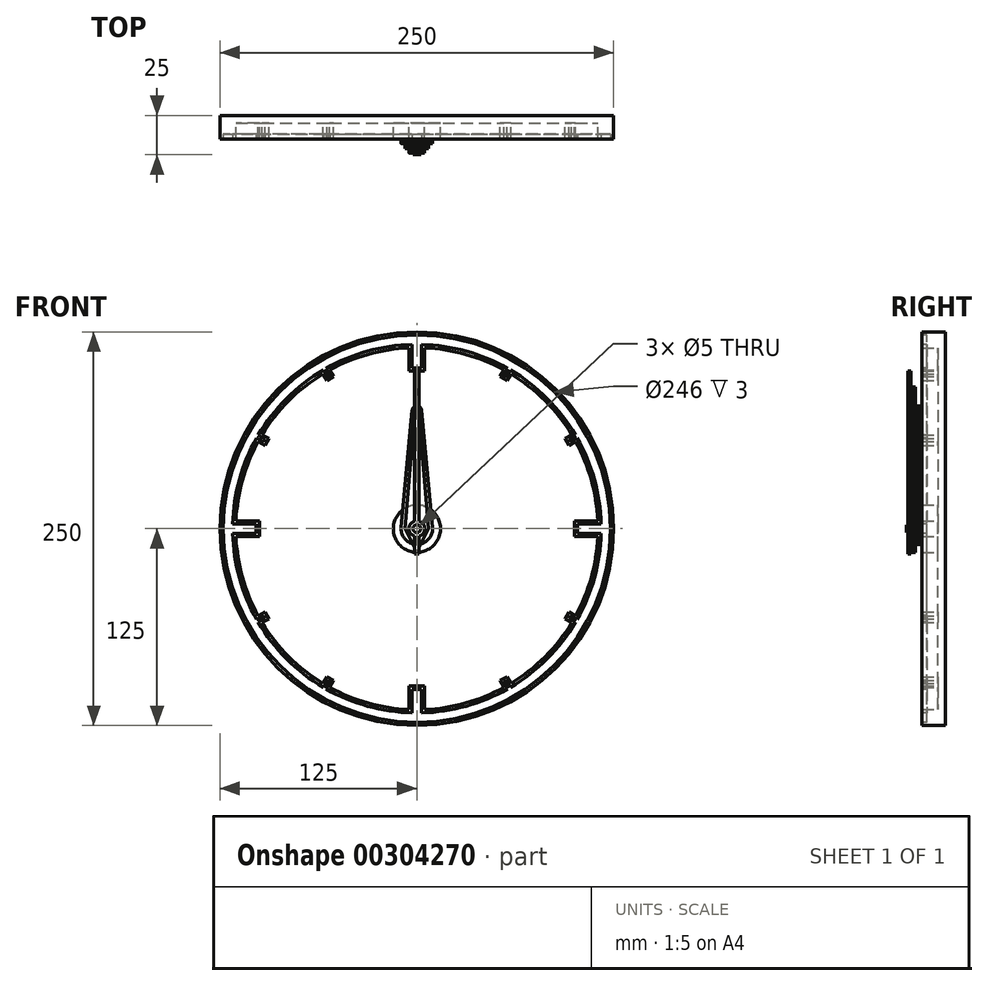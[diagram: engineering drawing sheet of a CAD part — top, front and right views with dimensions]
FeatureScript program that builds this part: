
annotation { "Feature Type Name" : "Feature", "Feature Type Description" : "" }
export const myFeature = defineFeature(function(context is Context, id is Id, definition is map)
    precondition{}
    {
        {
            var Q0;
            Q0=qCreatedBy(makeId("Front.planeOp"),FACE);
            var sketch = newSketch(context, id + "F0", { "sketchPlane" : qUnion([Q0])});
            skCircle(sketch, "E0", {"center": v(0, 0) * mm, "radius": 125 * mm});
            skSolve(sketch);
        }
        {
            var Q0;
            Q0 = qSketchRegion(id + "F0", true);
            extrude(context, id + "F1", {"entities" : qUnion([Q0]), "oppositeDirection" : true, "depth" : 5 * mm});
        }
        {
            var Q0;
            Q0=makeQuery(id+"F1.opExtrude","CAP_FACE",FACE,{"disambiguationData":[OSD([sQuery(id+"F0.wireOp",EDGE,"E0")])],"isStart":true});
            var sketch = newSketch(context, id + "F2", { "sketchPlane" : qUnion([Q0])});
            skCircle(sketch, "E1", {"center": v(0, 0) * mm, "radius": 15 * mm});
            skSolve(sketch);
        }
        {
            var Q0;
            Q0 = qSketchRegion(id + "F2", true);
            extrude(context, id + "F3", {"entities" : qUnion([Q0]), "depth" : 10 * mm});
        }
        {
            var Q0;
            Q0=makeQuery(id+"F3.opExtrude","CAP_FACE",FACE,{"disambiguationData":[OSD([sQuery(id+"F2.wireOp",EDGE,"E1")])],"isStart":false});
            var sketch = newSketch(context, id + "F4", { "sketchPlane" : qUnion([Q0])});
            skCircle(sketch, "E2", {"center": v(0, 0) * mm, "radius": 2.5 * mm});
            skSolve(sketch);
        }
        {
            var Q0;
            Q0 = qSketchRegion(id + "F4", true);
            extrude(context, id + "F5", {"entities" : qUnion([Q0]), "operationType" : NewBodyOperationType.ADD, "depth" : 10 * mm});
        }
        {
            var Q0;
            Q0=makeQuery(id+"F1.opExtrude","CAP_FACE",FACE,{"disambiguationData":[OSD([sQuery(id+"F0.wireOp",EDGE,"E0")])],"isStart":true});
            var sketch = newSketch(context, id + "F6", { "sketchPlane" : qUnion([Q0])});
            skCircle(sketch, "E3.0", {"center": v(0, 0) * mm, "radius": 125 * mm});
            skCircle(sketch, "E4", {"center": v(0, 0) * mm, "radius": 115 * mm});
            skSolve(sketch);
        }
        {
            var Q0;
            Q0 = qSketchRegion(id + "F6", true);
            extrude(context, id + "F7", {"entities" : qUnion([Q0]), "depth" : 10 * mm});
        }
        {
            var Q0;
            Q0=makeQuery(id+"F1.opExtrude","CAP_FACE",FACE,{"disambiguationData":[OSD([sQuery(id+"F0.wireOp",EDGE,"E0")])],"isStart":true});
            var sketch = newSketch(context, id + "F8", { "sketchPlane" : qUnion([Q0])});
            skLineSegment(sketch, "E5.bottom", {"start": v(5, 100) * mm, "end": v(-5, 100) * mm});
            skLineSegment(sketch, "E5.top", {"start": v(5, 120) * mm, "end": v(-5, 120) * mm});
            skLineSegment(sketch, "E5.left", {"start": v(5, 100) * mm, "end": v(5, 120) * mm});
            skLineSegment(sketch, "E5.right", {"start": v(-5, 100) * mm, "end": v(-5, 120) * mm});
            skPoint(sketch, "E5.middle", {"position": v(0, 110) * mm});
            skLineSegment(sketch, "E6.1.0", {"start": v(-100, 5) * mm, "end": v(-100, -5) * mm});
            skLineSegment(sketch, "E6.1.1", {"start": v(-120, 5) * mm, "end": v(-120, -5) * mm});
            skLineSegment(sketch, "E6.1.2", {"start": v(-100, 5) * mm, "end": v(-120, 5) * mm});
            skLineSegment(sketch, "E6.1.3", {"start": v(-100, -5) * mm, "end": v(-120, -5) * mm});
            skPoint(sketch, "E6.1.4", {"position": v(-110, 0) * mm});
            skLineSegment(sketch, "E6.2.0", {"start": v(-5, -100) * mm, "end": v(5, -100) * mm});
            skLineSegment(sketch, "E6.2.1", {"start": v(-5, -120) * mm, "end": v(5, -120) * mm});
            skLineSegment(sketch, "E6.2.2", {"start": v(-5, -100) * mm, "end": v(-5, -120) * mm});
            skLineSegment(sketch, "E6.2.3", {"start": v(5, -100) * mm, "end": v(5, -120) * mm});
            skPoint(sketch, "E6.2.4", {"position": v(0, -110) * mm});
            skLineSegment(sketch, "E6.3.0", {"start": v(100, -5) * mm, "end": v(100, 5) * mm});
            skLineSegment(sketch, "E6.3.1", {"start": v(120, -5) * mm, "end": v(120, 5) * mm});
            skLineSegment(sketch, "E6.3.2", {"start": v(100, -5) * mm, "end": v(120, -5) * mm});
            skLineSegment(sketch, "E6.3.3", {"start": v(100, 5) * mm, "end": v(120, 5) * mm});
            skPoint(sketch, "E6.3.4", {"position": v(110, 0) * mm});
            skPoint(sketch, "E6.center", {"position": v(0, 0) * mm});
            skSolve(sketch);
        }
        {
            var Q0;
            Q0 = qSketchRegion(id + "F8", true);
            extrude(context, id + "F9", {"entities" : qUnion([Q0]), "operationType" : NewBodyOperationType.ADD, "depth" : 10 * mm});
        }
        {
            var Q0;
            Q0=makeQuery(id+"F1.opExtrude","CAP_FACE",FACE,{"disambiguationData":[OSD([sQuery(id+"F0.wireOp",EDGE,"E0")])],"isStart":true});
            var sketch = newSketch(context, id + "F10", { "sketchPlane" : qUnion([Q0])});
            skLineSegment(sketch, "E7", {"start": v(0, 0) * mm, "end": v(0, 87.81) * mm, "construction": true});
            skLineSegment(sketch, "E8", {"start": v(0, 0) * mm, "end": v(55, 95.26) * mm, "construction": true});
            skLineSegment(sketch, "E9", {"start": v(0, 0) * mm, "end": v(95.26, 55) * mm, "construction": true});
            skLineSegment(sketch, "E10", {"start": v(57.83, 105.17) * mm, "end": v(52.83, 96.51) * mm});
            skLineSegment(sketch, "E11", {"start": v(52.83, 96.51) * mm, "end": v(57.17, 94.01) * mm});
            skLineSegment(sketch, "E12", {"start": v(57.17, 94.01) * mm, "end": v(62.17, 102.67) * mm});
            skLineSegment(sketch, "E13", {"start": v(62.17, 102.67) * mm, "end": v(57.83, 105.17) * mm});
            skLineSegment(sketch, "E14", {"start": v(102.67, 62.17) * mm, "end": v(94.01, 57.17) * mm});
            skLineSegment(sketch, "E15", {"start": v(94.01, 57.17) * mm, "end": v(96.51, 52.83) * mm});
            skLineSegment(sketch, "E16", {"start": v(96.51, 52.83) * mm, "end": v(105.17, 57.83) * mm});
            skLineSegment(sketch, "E17", {"start": v(105.17, 57.83) * mm, "end": v(102.67, 62.17) * mm});
            skLineSegment(sketch, "E18.1.0", {"start": v(-105.17, 57.83) * mm, "end": v(-96.51, 52.83) * mm});
            skLineSegment(sketch, "E18.1.1", {"start": v(-96.51, 52.83) * mm, "end": v(-94.01, 57.17) * mm});
            skLineSegment(sketch, "E18.1.2", {"start": v(-94.01, 57.17) * mm, "end": v(-102.67, 62.17) * mm});
            skLineSegment(sketch, "E18.1.3", {"start": v(-102.67, 62.17) * mm, "end": v(-105.17, 57.83) * mm});
            skLineSegment(sketch, "E18.1.4", {"start": v(-62.17, 102.67) * mm, "end": v(-57.17, 94.01) * mm});
            skLineSegment(sketch, "E18.1.5", {"start": v(-57.17, 94.01) * mm, "end": v(-52.83, 96.51) * mm});
            skLineSegment(sketch, "E18.1.6", {"start": v(-57.83, 105.17) * mm, "end": v(-62.17, 102.67) * mm});
            skLineSegment(sketch, "E18.1.7", {"start": v(-52.83, 96.51) * mm, "end": v(-57.83, 105.17) * mm});
            skLineSegment(sketch, "E18.2.0", {"start": v(-57.83, -105.17) * mm, "end": v(-52.83, -96.51) * mm});
            skLineSegment(sketch, "E18.2.1", {"start": v(-52.83, -96.51) * mm, "end": v(-57.17, -94.01) * mm});
            skLineSegment(sketch, "E18.2.2", {"start": v(-57.17, -94.01) * mm, "end": v(-62.17, -102.67) * mm});
            skLineSegment(sketch, "E18.2.3", {"start": v(-62.17, -102.67) * mm, "end": v(-57.83, -105.17) * mm});
            skLineSegment(sketch, "E18.2.4", {"start": v(-102.67, -62.17) * mm, "end": v(-94.01, -57.17) * mm});
            skLineSegment(sketch, "E18.2.5", {"start": v(-94.01, -57.17) * mm, "end": v(-96.51, -52.83) * mm});
            skLineSegment(sketch, "E18.2.6", {"start": v(-105.17, -57.83) * mm, "end": v(-102.67, -62.17) * mm});
            skLineSegment(sketch, "E18.2.7", {"start": v(-96.51, -52.83) * mm, "end": v(-105.17, -57.83) * mm});
            skLineSegment(sketch, "E18.3.0", {"start": v(105.17, -57.83) * mm, "end": v(96.51, -52.83) * mm});
            skLineSegment(sketch, "E18.3.1", {"start": v(96.51, -52.83) * mm, "end": v(94.01, -57.17) * mm});
            skLineSegment(sketch, "E18.3.2", {"start": v(94.01, -57.17) * mm, "end": v(102.67, -62.17) * mm});
            skLineSegment(sketch, "E18.3.3", {"start": v(102.67, -62.17) * mm, "end": v(105.17, -57.83) * mm});
            skLineSegment(sketch, "E18.3.4", {"start": v(62.17, -102.67) * mm, "end": v(57.17, -94.01) * mm});
            skLineSegment(sketch, "E18.3.5", {"start": v(57.17, -94.01) * mm, "end": v(52.83, -96.51) * mm});
            skLineSegment(sketch, "E18.3.6", {"start": v(57.83, -105.17) * mm, "end": v(62.17, -102.67) * mm});
            skLineSegment(sketch, "E18.3.7", {"start": v(52.83, -96.51) * mm, "end": v(57.83, -105.17) * mm});
            skPoint(sketch, "E18.center", {"position": v(0, 0) * mm});
            skSolve(sketch);
        }
        {
            var Q0;
            Q0 = qSketchRegion(id + "F10", true);
            extrude(context, id + "F11", {"entities" : qUnion([Q0]), "operationType" : NewBodyOperationType.ADD, "depth" : 10 * mm});
        }
        {
            var Q0;
            Q0=makeQuery(id+"F11.boolean.opBoolean","MERGE",FACE,{"derivedFrom":[makeQuery(id+"F9.boolean.opBoolean","MERGE",FACE,{"derivedFrom":[makeQuery(id+"F7.opExtrude","CAP_FACE",FACE,{"disambiguationData":[OSD([sQuery(id+"F6.wireOp",EDGE,"E3.0"),sQuery(id+"F6.wireOp",EDGE,"E4")])],"isStart":false}),makeQuery(id+"F9.opExtrude","CAP_FACE",FACE,{"disambiguationData":[OSD([sQuery(id+"F8.wireOp",EDGE,"E5.bottom"),sQuery(id+"F8.wireOp",EDGE,"E5.top"),sQuery(id+"F8.wireOp",EDGE,"E5.left"),sQuery(id+"F8.wireOp",EDGE,"E5.right")])],"isStart":false}),makeQuery(id+"F9.opExtrude","CAP_FACE",FACE,{"disambiguationData":[OSD([sQuery(id+"F8.wireOp",EDGE,"E6.1.0"),sQuery(id+"F8.wireOp",EDGE,"E6.1.1"),sQuery(id+"F8.wireOp",EDGE,"E6.1.2"),sQuery(id+"F8.wireOp",EDGE,"E6.1.3")])],"isStart":false}),makeQuery(id+"F9.opExtrude","CAP_FACE",FACE,{"disambiguationData":[OSD([sQuery(id+"F8.wireOp",EDGE,"E6.2.0"),sQuery(id+"F8.wireOp",EDGE,"E6.2.1"),sQuery(id+"F8.wireOp",EDGE,"E6.2.2"),sQuery(id+"F8.wireOp",EDGE,"E6.2.3")])],"isStart":false}),makeQuery(id+"F9.opExtrude","CAP_FACE",FACE,{"disambiguationData":[OSD([sQuery(id+"F8.wireOp",EDGE,"E6.3.0"),sQuery(id+"F8.wireOp",EDGE,"E6.3.1"),sQuery(id+"F8.wireOp",EDGE,"E6.3.2"),sQuery(id+"F8.wireOp",EDGE,"E6.3.3")])],"isStart":false})]}),makeQuery(id+"F11.opExtrude","CAP_FACE",FACE,{"disambiguationData":[OSD([sQuery(id+"F10.wireOp",EDGE,"E10"),sQuery(id+"F10.wireOp",EDGE,"E11"),sQuery(id+"F10.wireOp",EDGE,"E12"),sQuery(id+"F10.wireOp",EDGE,"E13")])],"isStart":false}),makeQuery(id+"F11.opExtrude","CAP_FACE",FACE,{"disambiguationData":[OSD([sQuery(id+"F10.wireOp",EDGE,"E14"),sQuery(id+"F10.wireOp",EDGE,"E15"),sQuery(id+"F10.wireOp",EDGE,"E16"),sQuery(id+"F10.wireOp",EDGE,"E17")])],"isStart":false}),makeQuery(id+"F11.opExtrude","CAP_FACE",FACE,{"disambiguationData":[OSD([sQuery(id+"F10.wireOp",EDGE,"E18.1.0"),sQuery(id+"F10.wireOp",EDGE,"E18.1.1"),sQuery(id+"F10.wireOp",EDGE,"E18.1.2"),sQuery(id+"F10.wireOp",EDGE,"E18.1.3")])],"isStart":false}),makeQuery(id+"F11.opExtrude","CAP_FACE",FACE,{"disambiguationData":[OSD([sQuery(id+"F10.wireOp",EDGE,"E18.1.4"),sQuery(id+"F10.wireOp",EDGE,"E18.1.5"),sQuery(id+"F10.wireOp",EDGE,"E18.1.6"),sQuery(id+"F10.wireOp",EDGE,"E18.1.7")])],"isStart":false}),makeQuery(id+"F11.opExtrude","CAP_FACE",FACE,{"disambiguationData":[OSD([sQuery(id+"F10.wireOp",EDGE,"E18.2.0"),sQuery(id+"F10.wireOp",EDGE,"E18.2.1"),sQuery(id+"F10.wireOp",EDGE,"E18.2.2"),sQuery(id+"F10.wireOp",EDGE,"E18.2.3")])],"isStart":false}),makeQuery(id+"F11.opExtrude","CAP_FACE",FACE,{"disambiguationData":[OSD([sQuery(id+"F10.wireOp",EDGE,"E18.2.4"),sQuery(id+"F10.wireOp",EDGE,"E18.2.5"),sQuery(id+"F10.wireOp",EDGE,"E18.2.6"),sQuery(id+"F10.wireOp",EDGE,"E18.2.7")])],"isStart":false}),makeQuery(id+"F11.opExtrude","CAP_FACE",FACE,{"disambiguationData":[OSD([sQuery(id+"F10.wireOp",EDGE,"E18.3.0"),sQuery(id+"F10.wireOp",EDGE,"E18.3.1"),sQuery(id+"F10.wireOp",EDGE,"E18.3.2"),sQuery(id+"F10.wireOp",EDGE,"E18.3.3")])],"isStart":false}),makeQuery(id+"F11.opExtrude","CAP_FACE",FACE,{"disambiguationData":[OSD([sQuery(id+"F10.wireOp",EDGE,"E18.3.4"),sQuery(id+"F10.wireOp",EDGE,"E18.3.5"),sQuery(id+"F10.wireOp",EDGE,"E18.3.6"),sQuery(id+"F10.wireOp",EDGE,"E18.3.7")])],"isStart":false})]});
            var sketch = newSketch(context, id + "F12", { "sketchPlane" : qUnion([Q0])});
            skCircle(sketch, "E19", {"center": v(0, 0) * mm, "radius": 123 * mm});
            skCircle(sketch, "E20", {"center": v(0, 0) * mm, "radius": 117 * mm});
            skSolve(sketch);
        }
        {
            var Q0;
            Q0 = qSketchRegion(id + "F12", true);
            extrude(context, id + "F13", {"entities" : qUnion([Q0]), "operationType" : NewBodyOperationType.REMOVE, "oppositeDirection" : true, "depth" : 3 * mm});
        }
        {
            var Q0;
            {var subQ0=sQuery(id+"F10.wireOp",EDGE,"E18.1.0");var subQ1=sQuery(id+"F8.wireOp",EDGE,"E6.3.0");var subQ2=sQuery(id+"F10.wireOp",EDGE,"E14");var subQ3=sQuery(id+"F8.wireOp",EDGE,"E6.2.0");var subQ4=sQuery(id+"F10.wireOp",EDGE,"E15");var subQ5=sQuery(id+"F8.wireOp",EDGE,"E6.3.2");var subQ6=sQuery(id+"F10.wireOp",EDGE,"E18.1.2");var subQ7=sQuery(id+"F10.wireOp",EDGE,"E18.1.1");var subQ8=sQuery(id+"F8.wireOp",EDGE,"E5.right");var subQ9=sQuery(id+"F10.wireOp",EDGE,"E11");var subQ10=sQuery(id+"F8.wireOp",EDGE,"E6.2.2");var subQ11=sQuery(id+"F10.wireOp",EDGE,"E16");var subQ12=sQuery(id+"F8.wireOp",EDGE,"E6.3.3");var subQ13=sQuery(id+"F8.wireOp",EDGE,"E5.bottom");var subQ14=sQuery(id+"F8.wireOp",EDGE,"E6.1.3");var subQ15=sQuery(id+"F8.wireOp",EDGE,"E5.left");var subQ16=sQuery(id+"F10.wireOp",EDGE,"E18.3.5");var subQ17=sQuery(id+"F10.wireOp",EDGE,"E10");var subQ18=sQuery(id+"F8.wireOp",EDGE,"E6.1.0");var subQ19=sQuery(id+"F10.wireOp",EDGE,"E18.3.7");var subQ20=sQuery(id+"F6.wireOp",EDGE,"E4");var subQ21=sQuery(id+"F10.wireOp",EDGE,"E12");var subQ22=sQuery(id+"F8.wireOp",EDGE,"E6.1.2");var subQ23=sQuery(id+"F8.wireOp",EDGE,"E6.2.3");var subQ24=sQuery(id+"F10.wireOp",EDGE,"E18.1.4");var subQ25=sQuery(id+"F10.wireOp",EDGE,"E18.1.5");var subQ26=sQuery(id+"F10.wireOp",EDGE,"E18.1.7");var subQ27=sQuery(id+"F10.wireOp",EDGE,"E18.2.0");var subQ28=sQuery(id+"F10.wireOp",EDGE,"E18.2.1");var subQ29=sQuery(id+"F10.wireOp",EDGE,"E18.2.2");var subQ30=sQuery(id+"F10.wireOp",EDGE,"E18.2.4");var subQ31=sQuery(id+"F10.wireOp",EDGE,"E18.2.5");var subQ32=sQuery(id+"F10.wireOp",EDGE,"E18.2.7");var subQ33=sQuery(id+"F10.wireOp",EDGE,"E18.3.0");var subQ34=sQuery(id+"F10.wireOp",EDGE,"E18.3.1");var subQ35=sQuery(id+"F10.wireOp",EDGE,"E18.3.2");var subQ36=sQuery(id+"F10.wireOp",EDGE,"E18.3.4");Q0=makeQuery(id+"F13.boolean.opBoolean","SPLIT",FACE,{"disambiguationData":[TD([makeQuery(id+"F7.opExtrude","SWEPT_FACE",FACE,{"disambiguationData":[OSD([subQ20])]})])],"derivedFrom":makeQuery(id+"F11.boolean.opBoolean","MERGE",FACE,{"derivedFrom":[makeQuery(id+"F9.boolean.opBoolean","MERGE",FACE,{"derivedFrom":[makeQuery(id+"F7.opExtrude","CAP_FACE",FACE,{"disambiguationData":[OSD([sQuery(id+"F6.wireOp",EDGE,"E3.0"),subQ20])],"isStart":false}),makeQuery(id+"F9.opExtrude","CAP_FACE",FACE,{"disambiguationData":[OSD([subQ13,sQuery(id+"F8.wireOp",EDGE,"E5.top"),subQ15,subQ8])],"isStart":false}),makeQuery(id+"F9.opExtrude","CAP_FACE",FACE,{"disambiguationData":[OSD([subQ18,sQuery(id+"F8.wireOp",EDGE,"E6.1.1"),subQ22,subQ14])],"isStart":false}),makeQuery(id+"F9.opExtrude","CAP_FACE",FACE,{"disambiguationData":[OSD([subQ3,sQuery(id+"F8.wireOp",EDGE,"E6.2.1"),subQ10,subQ23])],"isStart":false}),makeQuery(id+"F9.opExtrude","CAP_FACE",FACE,{"disambiguationData":[OSD([subQ1,sQuery(id+"F8.wireOp",EDGE,"E6.3.1"),subQ5,subQ12])],"isStart":false})]}),makeQuery(id+"F11.opExtrude","CAP_FACE",FACE,{"disambiguationData":[OSD([subQ17,subQ9,subQ21,sQuery(id+"F10.wireOp",EDGE,"E13")])],"isStart":false}),makeQuery(id+"F11.opExtrude","CAP_FACE",FACE,{"disambiguationData":[OSD([subQ2,subQ4,subQ11,sQuery(id+"F10.wireOp",EDGE,"E17")])],"isStart":false}),makeQuery(id+"F11.opExtrude","CAP_FACE",FACE,{"disambiguationData":[OSD([subQ0,subQ7,subQ6,sQuery(id+"F10.wireOp",EDGE,"E18.1.3")])],"isStart":false}),makeQuery(id+"F11.opExtrude","CAP_FACE",FACE,{"disambiguationData":[OSD([subQ24,subQ25,sQuery(id+"F10.wireOp",EDGE,"E18.1.6"),subQ26])],"isStart":false}),makeQuery(id+"F11.opExtrude","CAP_FACE",FACE,{"disambiguationData":[OSD([subQ27,subQ28,subQ29,sQuery(id+"F10.wireOp",EDGE,"E18.2.3")])],"isStart":false}),makeQuery(id+"F11.opExtrude","CAP_FACE",FACE,{"disambiguationData":[OSD([subQ30,subQ31,sQuery(id+"F10.wireOp",EDGE,"E18.2.6"),subQ32])],"isStart":false}),makeQuery(id+"F11.opExtrude","CAP_FACE",FACE,{"disambiguationData":[OSD([subQ33,subQ34,subQ35,sQuery(id+"F10.wireOp",EDGE,"E18.3.3")])],"isStart":false}),makeQuery(id+"F11.opExtrude","CAP_FACE",FACE,{"disambiguationData":[OSD([subQ36,subQ16,sQuery(id+"F10.wireOp",EDGE,"E18.3.6"),subQ19])],"isStart":false})]})});}
            var sketch = newSketch(context, id + "F14", { "sketchPlane" : qUnion([Q0])});
            skLineSegment(sketch, "E21.bottom", {"start": v(3, 102) * mm, "end": v(-3, 102) * mm});
            skLineSegment(sketch, "E21.top", {"start": v(3, 120) * mm, "end": v(-3, 120) * mm});
            skLineSegment(sketch, "E21.left", {"start": v(3, 102) * mm, "end": v(3, 120) * mm});
            skLineSegment(sketch, "E21.right", {"start": v(-3, 102) * mm, "end": v(-3, 120) * mm});
            skPoint(sketch, "E21.middle", {"position": v(0, 111) * mm});
            skPoint(sketch, "E22.1.0", {"position": v(-111, 0) * mm});
            skLineSegment(sketch, "E22.1.1", {"start": v(-102, -3) * mm, "end": v(-120, -3) * mm});
            skLineSegment(sketch, "E22.1.2", {"start": v(-102, 3) * mm, "end": v(-120, 3) * mm});
            skLineSegment(sketch, "E22.1.3", {"start": v(-120, 3) * mm, "end": v(-120, -3) * mm});
            skLineSegment(sketch, "E22.1.4", {"start": v(-102, 3) * mm, "end": v(-102, -3) * mm});
            skPoint(sketch, "E22.2.0", {"position": v(0, -111) * mm});
            skLineSegment(sketch, "E22.2.1", {"start": v(3, -102) * mm, "end": v(3, -120) * mm});
            skLineSegment(sketch, "E22.2.2", {"start": v(-3, -102) * mm, "end": v(-3, -120) * mm});
            skLineSegment(sketch, "E22.2.3", {"start": v(-3, -120) * mm, "end": v(3, -120) * mm});
            skLineSegment(sketch, "E22.2.4", {"start": v(-3, -102) * mm, "end": v(3, -102) * mm});
            skPoint(sketch, "E22.3.0", {"position": v(111, 0) * mm});
            skLineSegment(sketch, "E22.3.1", {"start": v(102, 3) * mm, "end": v(120, 3) * mm});
            skLineSegment(sketch, "E22.3.2", {"start": v(102, -3) * mm, "end": v(120, -3) * mm});
            skLineSegment(sketch, "E22.3.3", {"start": v(120, -3) * mm, "end": v(120, 3) * mm});
            skLineSegment(sketch, "E22.3.4", {"start": v(102, -3) * mm, "end": v(102, 3) * mm});
            skPoint(sketch, "E22.center", {"position": v(0, 0) * mm});
            skSolve(sketch);
        }
        {
            var Q0;
            Q0 = qSketchRegion(id + "F14", true);
            extrude(context, id + "F15", {"entities" : qUnion([Q0]), "operationType" : NewBodyOperationType.REMOVE, "oppositeDirection" : true, "depth" : 3 * mm});
        }
        {
            var Q0;
            {var subQ0=sQuery(id+"F10.wireOp",EDGE,"E18.1.0");var subQ1=sQuery(id+"F8.wireOp",EDGE,"E6.3.0");var subQ2=sQuery(id+"F10.wireOp",EDGE,"E14");var subQ3=sQuery(id+"F8.wireOp",EDGE,"E6.2.0");var subQ4=sQuery(id+"F10.wireOp",EDGE,"E15");var subQ5=sQuery(id+"F8.wireOp",EDGE,"E6.3.2");var subQ6=sQuery(id+"F10.wireOp",EDGE,"E18.1.2");var subQ7=sQuery(id+"F10.wireOp",EDGE,"E18.1.1");var subQ8=sQuery(id+"F8.wireOp",EDGE,"E5.right");var subQ9=sQuery(id+"F10.wireOp",EDGE,"E11");var subQ10=sQuery(id+"F8.wireOp",EDGE,"E6.2.2");var subQ11=sQuery(id+"F10.wireOp",EDGE,"E16");var subQ12=sQuery(id+"F8.wireOp",EDGE,"E6.3.3");var subQ13=sQuery(id+"F8.wireOp",EDGE,"E5.bottom");var subQ14=sQuery(id+"F8.wireOp",EDGE,"E6.1.3");var subQ15=sQuery(id+"F8.wireOp",EDGE,"E5.left");var subQ16=sQuery(id+"F10.wireOp",EDGE,"E18.3.5");var subQ17=sQuery(id+"F10.wireOp",EDGE,"E10");var subQ18=sQuery(id+"F8.wireOp",EDGE,"E6.1.0");var subQ19=sQuery(id+"F10.wireOp",EDGE,"E18.3.7");var subQ20=sQuery(id+"F6.wireOp",EDGE,"E4");var subQ21=sQuery(id+"F10.wireOp",EDGE,"E12");var subQ22=sQuery(id+"F8.wireOp",EDGE,"E6.1.2");var subQ23=sQuery(id+"F8.wireOp",EDGE,"E6.2.3");var subQ24=sQuery(id+"F10.wireOp",EDGE,"E18.1.4");var subQ25=sQuery(id+"F10.wireOp",EDGE,"E18.1.5");var subQ26=sQuery(id+"F10.wireOp",EDGE,"E18.1.7");var subQ27=sQuery(id+"F10.wireOp",EDGE,"E18.2.0");var subQ28=sQuery(id+"F10.wireOp",EDGE,"E18.2.1");var subQ29=sQuery(id+"F10.wireOp",EDGE,"E18.2.2");var subQ30=sQuery(id+"F10.wireOp",EDGE,"E18.2.4");var subQ31=sQuery(id+"F10.wireOp",EDGE,"E18.2.5");var subQ32=sQuery(id+"F10.wireOp",EDGE,"E18.2.7");var subQ33=sQuery(id+"F10.wireOp",EDGE,"E18.3.0");var subQ34=sQuery(id+"F10.wireOp",EDGE,"E18.3.1");var subQ35=sQuery(id+"F10.wireOp",EDGE,"E18.3.2");var subQ36=sQuery(id+"F10.wireOp",EDGE,"E18.3.4");Q0=makeQuery(id+"F13.boolean.opBoolean","SPLIT",FACE,{"disambiguationData":[TD([makeQuery(id+"F7.opExtrude","SWEPT_FACE",FACE,{"disambiguationData":[OSD([subQ20])]})])],"derivedFrom":makeQuery(id+"F11.boolean.opBoolean","MERGE",FACE,{"derivedFrom":[makeQuery(id+"F9.boolean.opBoolean","MERGE",FACE,{"derivedFrom":[makeQuery(id+"F7.opExtrude","CAP_FACE",FACE,{"disambiguationData":[OSD([sQuery(id+"F6.wireOp",EDGE,"E3.0"),subQ20])],"isStart":false}),makeQuery(id+"F9.opExtrude","CAP_FACE",FACE,{"disambiguationData":[OSD([subQ13,sQuery(id+"F8.wireOp",EDGE,"E5.top"),subQ15,subQ8])],"isStart":false}),makeQuery(id+"F9.opExtrude","CAP_FACE",FACE,{"disambiguationData":[OSD([subQ18,sQuery(id+"F8.wireOp",EDGE,"E6.1.1"),subQ22,subQ14])],"isStart":false}),makeQuery(id+"F9.opExtrude","CAP_FACE",FACE,{"disambiguationData":[OSD([subQ3,sQuery(id+"F8.wireOp",EDGE,"E6.2.1"),subQ10,subQ23])],"isStart":false}),makeQuery(id+"F9.opExtrude","CAP_FACE",FACE,{"disambiguationData":[OSD([subQ1,sQuery(id+"F8.wireOp",EDGE,"E6.3.1"),subQ5,subQ12])],"isStart":false})]}),makeQuery(id+"F11.opExtrude","CAP_FACE",FACE,{"disambiguationData":[OSD([subQ17,subQ9,subQ21,sQuery(id+"F10.wireOp",EDGE,"E13")])],"isStart":false}),makeQuery(id+"F11.opExtrude","CAP_FACE",FACE,{"disambiguationData":[OSD([subQ2,subQ4,subQ11,sQuery(id+"F10.wireOp",EDGE,"E17")])],"isStart":false}),makeQuery(id+"F11.opExtrude","CAP_FACE",FACE,{"disambiguationData":[OSD([subQ0,subQ7,subQ6,sQuery(id+"F10.wireOp",EDGE,"E18.1.3")])],"isStart":false}),makeQuery(id+"F11.opExtrude","CAP_FACE",FACE,{"disambiguationData":[OSD([subQ24,subQ25,sQuery(id+"F10.wireOp",EDGE,"E18.1.6"),subQ26])],"isStart":false}),makeQuery(id+"F11.opExtrude","CAP_FACE",FACE,{"disambiguationData":[OSD([subQ27,subQ28,subQ29,sQuery(id+"F10.wireOp",EDGE,"E18.2.3")])],"isStart":false}),makeQuery(id+"F11.opExtrude","CAP_FACE",FACE,{"disambiguationData":[OSD([subQ30,subQ31,sQuery(id+"F10.wireOp",EDGE,"E18.2.6"),subQ32])],"isStart":false}),makeQuery(id+"F11.opExtrude","CAP_FACE",FACE,{"disambiguationData":[OSD([subQ33,subQ34,subQ35,sQuery(id+"F10.wireOp",EDGE,"E18.3.3")])],"isStart":false}),makeQuery(id+"F11.opExtrude","CAP_FACE",FACE,{"disambiguationData":[OSD([subQ36,subQ16,sQuery(id+"F10.wireOp",EDGE,"E18.3.6"),subQ19])],"isStart":false})]})});}
            var sketch = newSketch(context, id + "F16", { "sketchPlane" : qUnion([Q0])});
            skLineSegment(sketch, "E23", {"start": v(0, 0) * mm, "end": v(0, 98.67) * mm, "construction": true});
            skLineSegment(sketch, "E24", {"start": v(0, 0) * mm, "end": v(56, 97) * mm, "construction": true});
            skLineSegment(sketch, "E25", {"start": v(0, 0) * mm, "end": v(97, 56) * mm, "construction": true});
            skLineSegment(sketch, "E26", {"start": v(58.41, 103.17) * mm, "end": v(55.13, 97.5) * mm});
            skLineSegment(sketch, "E27", {"start": v(55.13, 97.5) * mm, "end": v(56.87, 96.5) * mm});
            skLineSegment(sketch, "E28", {"start": v(56.87, 96.5) * mm, "end": v(60.14, 102.17) * mm});
            skLineSegment(sketch, "E29", {"start": v(60.14, 102.17) * mm, "end": v(58.41, 103.17) * mm});
            skLineSegment(sketch, "E30", {"start": v(102.17, 60.14) * mm, "end": v(96.5, 56.87) * mm});
            skLineSegment(sketch, "E31", {"start": v(96.5, 56.87) * mm, "end": v(97.5, 55.13) * mm});
            skLineSegment(sketch, "E32", {"start": v(97.5, 55.13) * mm, "end": v(103.17, 58.41) * mm});
            skLineSegment(sketch, "E33", {"start": v(103.17, 58.41) * mm, "end": v(102.17, 60.14) * mm});
            skLineSegment(sketch, "E34.1.0", {"start": v(-58.41, 103.17) * mm, "end": v(-60.14, 102.17) * mm});
            skLineSegment(sketch, "E34.1.1", {"start": v(-55.13, 97.5) * mm, "end": v(-58.41, 103.17) * mm});
            skLineSegment(sketch, "E34.1.2", {"start": v(-56.87, 96.5) * mm, "end": v(-55.13, 97.5) * mm});
            skLineSegment(sketch, "E34.1.3", {"start": v(-60.14, 102.17) * mm, "end": v(-56.87, 96.5) * mm});
            skLineSegment(sketch, "E34.1.4", {"start": v(-102.17, 60.14) * mm, "end": v(-103.17, 58.41) * mm});
            skLineSegment(sketch, "E34.1.5", {"start": v(-96.5, 56.87) * mm, "end": v(-102.17, 60.14) * mm});
            skLineSegment(sketch, "E34.1.6", {"start": v(-97.5, 55.13) * mm, "end": v(-96.5, 56.87) * mm});
            skLineSegment(sketch, "E34.1.7", {"start": v(-103.17, 58.41) * mm, "end": v(-97.5, 55.13) * mm});
            skLineSegment(sketch, "E34.2.0", {"start": v(-103.17, -58.41) * mm, "end": v(-102.17, -60.14) * mm});
            skLineSegment(sketch, "E34.2.1", {"start": v(-97.5, -55.13) * mm, "end": v(-103.17, -58.41) * mm});
            skLineSegment(sketch, "E34.2.2", {"start": v(-96.5, -56.87) * mm, "end": v(-97.5, -55.13) * mm});
            skLineSegment(sketch, "E34.2.3", {"start": v(-102.17, -60.14) * mm, "end": v(-96.5, -56.87) * mm});
            skLineSegment(sketch, "E34.2.4", {"start": v(-60.14, -102.17) * mm, "end": v(-58.41, -103.17) * mm});
            skLineSegment(sketch, "E34.2.5", {"start": v(-56.87, -96.5) * mm, "end": v(-60.14, -102.17) * mm});
            skLineSegment(sketch, "E34.2.6", {"start": v(-55.13, -97.5) * mm, "end": v(-56.87, -96.5) * mm});
            skLineSegment(sketch, "E34.2.7", {"start": v(-58.41, -103.17) * mm, "end": v(-55.13, -97.5) * mm});
            skLineSegment(sketch, "E34.3.0", {"start": v(58.41, -103.17) * mm, "end": v(60.14, -102.17) * mm});
            skLineSegment(sketch, "E34.3.1", {"start": v(55.13, -97.5) * mm, "end": v(58.41, -103.17) * mm});
            skLineSegment(sketch, "E34.3.2", {"start": v(56.87, -96.5) * mm, "end": v(55.13, -97.5) * mm});
            skLineSegment(sketch, "E34.3.3", {"start": v(60.14, -102.17) * mm, "end": v(56.87, -96.5) * mm});
            skLineSegment(sketch, "E34.3.4", {"start": v(102.17, -60.14) * mm, "end": v(103.17, -58.41) * mm});
            skLineSegment(sketch, "E34.3.5", {"start": v(96.5, -56.87) * mm, "end": v(102.17, -60.14) * mm});
            skLineSegment(sketch, "E34.3.6", {"start": v(97.5, -55.13) * mm, "end": v(96.5, -56.87) * mm});
            skLineSegment(sketch, "E34.3.7", {"start": v(103.17, -58.41) * mm, "end": v(97.5, -55.13) * mm});
            skPoint(sketch, "E34.center", {"position": v(0, 0) * mm});
            skSolve(sketch);
        }
        {
            var Q0;
            Q0 = qSketchRegion(id + "F16", true);
            extrude(context, id + "F17", {"entities" : qUnion([Q0]), "operationType" : NewBodyOperationType.REMOVE, "oppositeDirection" : true, "depth" : 3 * mm});
        }
        {
            var Q0;
            Q0=makeQuery(id+"F3.opExtrude","CAP_FACE",FACE,{"disambiguationData":[OSD([sQuery(id+"F2.wireOp",EDGE,"E1")])],"isStart":false});
            cPlane(context, id + "F18", {"entities" : qUnion([Q0]), "cplaneType" : CPlaneType.OFFSET, "offset" : 1 * mm, "width" : 150 * mm, "height" : 150 * mm});
        }
        {
            var Q0;
            Q0=qCreatedBy(id+"F18.planeOp",FACE);
            var sketch = newSketch(context, id + "F19", { "sketchPlane" : qUnion([Q0])});
            skLineSegment(sketch, "E35", {"start": v(0, 0) * mm, "end": v(0, 78.77) * mm, "construction": true});
            skLineSegment(sketch, "E36", {"start": v(-2.99, 75.28) * mm, "end": v(-9.96, 0.93) * mm});
            skLineSegment(sketch, "E37", {"start": v(2.99, 75.28) * mm, "end": v(9.96, 0.93) * mm});
            skArc(sketch, "E38", {"start": v(-2.99, 75.28) * mm, "mid": v(0, 78) * mm, "end": v(2.99, 75.28) * mm});
            skArc(sketch, "E39", {"start": v(-9.96, 0.93) * mm, "mid": v(0, -10) * mm, "end": v(9.96, 0.93) * mm});
            skCircle(sketch, "E40.0", {"center": v(0, 0) * mm, "radius": 2.5 * mm});
            skSolve(sketch);
        }
        {
            var Q0;
            Q0 = qSketchRegion(id + "F19", true);
            extrude(context, id + "F20", {"entities" : qUnion([Q0]), "depth" : 2 * mm});
        }
        {
            var Q0;
            Q0=makeQuery(id+"F20.opExtrude","CAP_FACE",FACE,{"disambiguationData":[OSD([sQuery(id+"F19.wireOp",EDGE,"E36"),sQuery(id+"F19.wireOp",EDGE,"E37"),sQuery(id+"F19.wireOp",EDGE,"E38"),sQuery(id+"F19.wireOp",EDGE,"E39")])],"isStart":false});
            cPlane(context, id + "F21", {"entities" : qUnion([Q0]), "cplaneType" : CPlaneType.OFFSET, "offset" : 1 * mm, "width" : 150 * mm, "height" : 150 * mm});
        }
        {
            var Q0;
            Q0=qCreatedBy(id+"F21.planeOp",FACE);
            var sketch = newSketch(context, id + "F22", { "sketchPlane" : qUnion([Q0])});
            skLineSegment(sketch, "E41", {"start": v(0, 0) * mm, "end": v(0, 90) * mm, "construction": true});
            skLineSegment(sketch, "E42", {"start": v(0, 90) * mm, "end": v(-7.5, 0) * mm});
            skLineSegment(sketch, "E43", {"start": v(-7.5, 0) * mm, "end": v(0, -15) * mm});
            skLineSegment(sketch, "E44", {"start": v(0, -15) * mm, "end": v(7.5, 0) * mm});
            skLineSegment(sketch, "E45", {"start": v(7.5, 0) * mm, "end": v(0, 90) * mm});
            skCircle(sketch, "E46.0", {"center": v(0, 0) * mm, "radius": 2.5 * mm});
            skSolve(sketch);
        }
        {
            var Q0;
            Q0 = qSketchRegion(id + "F22", true);
            extrude(context, id + "F23", {"entities" : qUnion([Q0]), "depth" : 2 * mm});
        }
        {
            var Q0;
            Q0=makeQuery(id+"F23.opExtrude","CAP_FACE",FACE,{"disambiguationData":[OSD([sQuery(id+"F22.wireOp",EDGE,"E42"),sQuery(id+"F22.wireOp",EDGE,"E43"),sQuery(id+"F22.wireOp",EDGE,"E44"),sQuery(id+"F22.wireOp",EDGE,"E45"),sQuery(id+"F22.wireOp",EDGE,"E46.0")])],"isStart":false});
            cPlane(context, id + "F24", {"entities" : qUnion([Q0]), "cplaneType" : CPlaneType.OFFSET, "offset" : 1 * mm, "width" : 150 * mm, "height" : 150 * mm});
        }
        {
            var Q0;
            Q0=qCreatedBy(id+"F24.planeOp",FACE);
            var sketch = newSketch(context, id + "F25", { "sketchPlane" : qUnion([Q0])});
            skLineSegment(sketch, "E47", {"start": v(0, 0) * mm, "end": v(0, 100) * mm, "construction": true});
            skCircle(sketch, "E48.0", {"center": v(0, 0) * mm, "radius": 2.5 * mm});
            skArc(sketch, "E49", {"start": v(1.5, -4.77) * mm, "mid": v(5, 0) * mm, "end": v(1.5, 4.77) * mm});
            skLineSegment(sketch, "E50.bottom", {"start": v(1.5, 100) * mm, "end": v(-1.5, 100) * mm});
            skLineSegment(sketch, "E50.top", {"start": v(1.5, -16) * mm, "end": v(-1.5, -16) * mm});
            skLineSegment(sketch, "E50.left", {"start": v(1.5, 100) * mm, "end": v(1.5, 4.77) * mm});
            skLineSegment(sketch, "E50.right", {"start": v(-1.5, 100) * mm, "end": v(-1.5, 4.77) * mm});
            skPoint(sketch, "E50.middle", {"position": v(0, 42) * mm});
            skLineSegment(sketch, "E51.trimOffspring", {"start": v(-1.5, -4.77) * mm, "end": v(-1.5, -16) * mm});
            skLineSegment(sketch, "E52.trimOffspring", {"start": v(1.5, -4.77) * mm, "end": v(1.5, -16) * mm});
            skArc(sketch, "E53.trimOffspring", {"start": v(-1.5, 4.77) * mm, "mid": v(-5, 0) * mm, "end": v(-1.5, -4.77) * mm});
            skSolve(sketch);
        }
        {
            var Q0;
            Q0 = qSketchRegion(id + "F25", true);
            extrude(context, id + "F26", {"entities" : qUnion([Q0]), "depth" : 2 * mm});
        }
    });
